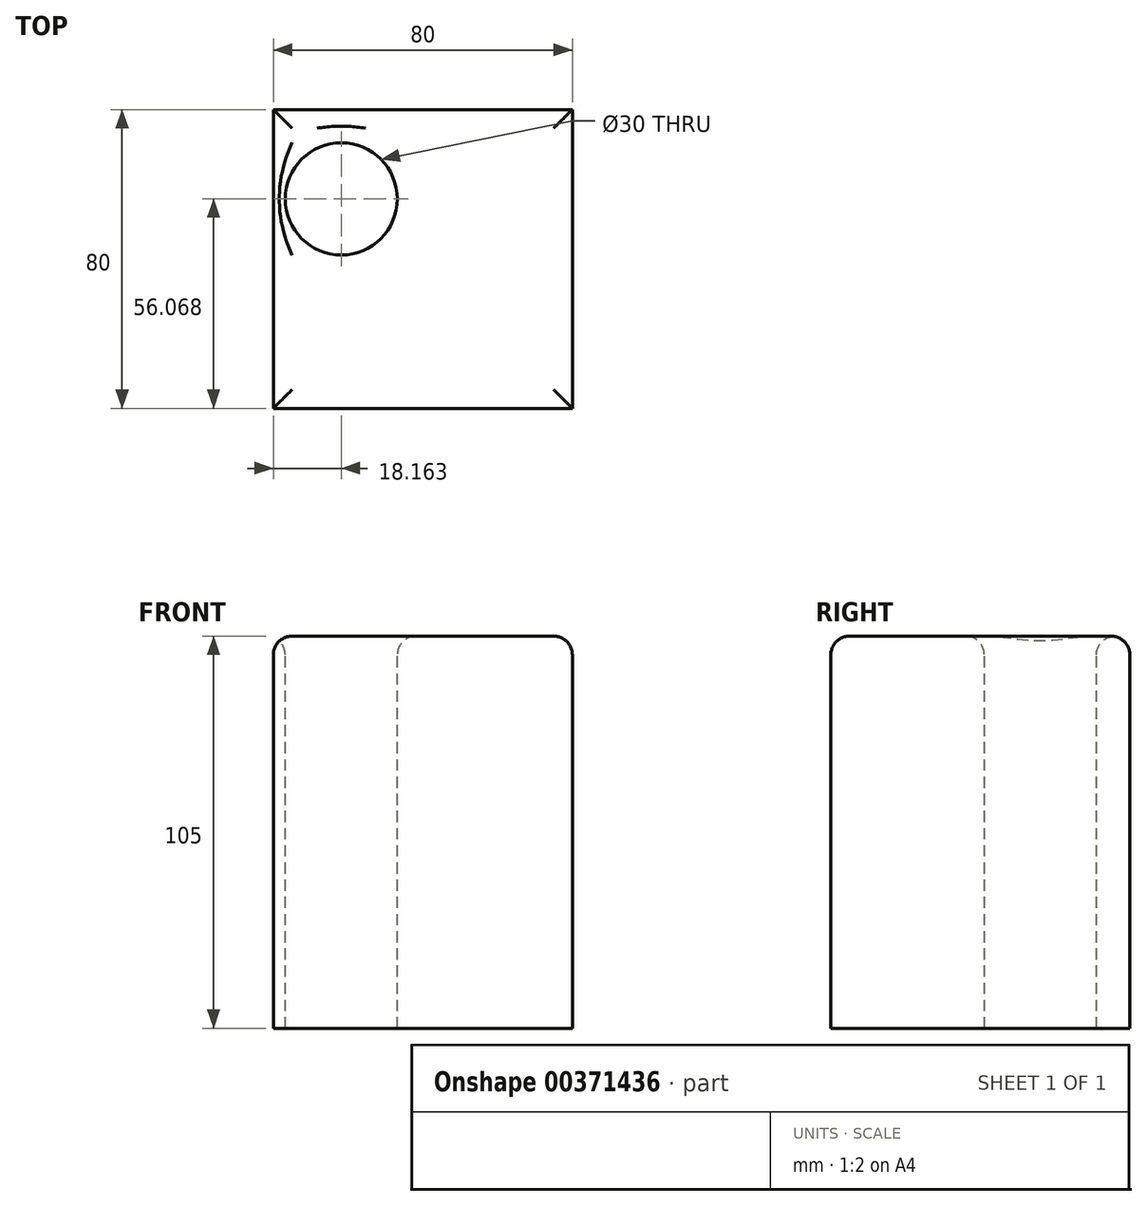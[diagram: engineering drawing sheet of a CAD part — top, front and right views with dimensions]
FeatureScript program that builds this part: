
annotation { "Feature Type Name" : "Feature", "Feature Type Description" : "" }
export const myFeature = defineFeature(function(context is Context, id is Id, definition is map)
    precondition{}
    {
        {
            var Q0;
            Q0=qCreatedBy(makeId("Top.planeOp"),FACE);
            var sketch = newSketch(context, id + "F0", { "sketchPlane" : qUnion([Q0])});
            skLineSegment(sketch, "E0.bottom", {"start": v(-141.9, 72.16) * mm, "end": v(-61.9, 72.16) * mm});
            skLineSegment(sketch, "E0.top", {"start": v(-141.9, -7.84) * mm, "end": v(-61.9, -7.84) * mm});
            skLineSegment(sketch, "E0.left", {"start": v(-141.9, 72.16) * mm, "end": v(-141.9, -7.84) * mm});
            skLineSegment(sketch, "E0.right", {"start": v(-61.9, 72.16) * mm, "end": v(-61.9, -7.84) * mm});
            skSolve(sketch);
        }
        {
            var Q0;
            Q0=makeQuery(id+"F0.imprint","IMPRINT",FACE,{"disambiguationData":[TD([[makeQuery(id+"F0.imprint","IMPRINT",EDGE,{"derivedFrom":sQuery(id+"F0.wireOp",EDGE,"E0.bottom")}),-1.0]])]});
            extrude(context, id + "F1", {"entities" : qUnion([Q0]), "depth" : 80 * mm});
        }
        {
            var Q0;
            Q0=makeQuery(id+"F1.opExtrude","CAP_FACE",FACE,{"disambiguationData":[OSD([sQuery(id+"F0.wireOp",EDGE,"E0.bottom"),sQuery(id+"F0.wireOp",EDGE,"E0.top"),sQuery(id+"F0.wireOp",EDGE,"E0.left"),sQuery(id+"F0.wireOp",EDGE,"E0.right")])],"isStart":false});
            extrude(context, id + "F2", {"entities" : qUnion([Q0]), "operationType" : NewBodyOperationType.ADD, "depth" : 25 * mm});
        }
        {
            var Q0;
            Q0=makeQuery(id+"F2.opExtrude","CAP_FACE",FACE,{"disambiguationData":[OSD([sQuery(id+"F0.wireOp",EDGE,"E0.bottom"),sQuery(id+"F0.wireOp",EDGE,"E0.top"),sQuery(id+"F0.wireOp",EDGE,"E0.left"),sQuery(id+"F0.wireOp",EDGE,"E0.right")])],"isStart":false});
            var sketch = newSketch(context, id + "F3", { "sketchPlane" : qUnion([Q0])});
            skCircle(sketch, "E1", {"center": v(-123.73, 48.23) * mm, "radius": 15 * mm});
            skSolve(sketch);
        }
        {
            var Q0;
            Q0=makeQuery(id+"F3.imprint","IMPRINT",FACE,{"disambiguationData":[TD([[makeQuery(id+"F3.imprint","IMPRINT",EDGE,{"derivedFrom":sQuery(id+"F3.wireOp",EDGE,"E1")}),1.0]])]});
            extrude(context, id + "F4", {"entities" : qUnion([Q0]), "operationType" : NewBodyOperationType.REMOVE, "endBound" : BoundingType.THROUGH_ALL, "oppositeDirection" : true, "depth" : 25 * mm});
        }
        {
            var Q0;
            Q0=makeQuery(id+"F4.boolean.opBoolean","COPY",EDGE,{"derivedFrom":makeQuery(id+"F4.opExtrude","CAP_EDGE",EDGE,{"disambiguationData":[OSD([sQuery(id+"F3.wireOp",EDGE,"E1")])],"isStart":true})});
            var Q1;
            Q1=makeQuery(id+"F2.opExtrude","CAP_FACE",FACE,{"disambiguationData":[OSD([sQuery(id+"F0.wireOp",EDGE,"E0.bottom"),sQuery(id+"F0.wireOp",EDGE,"E0.top"),sQuery(id+"F0.wireOp",EDGE,"E0.left"),sQuery(id+"F0.wireOp",EDGE,"E0.right")])],"isStart":false});
            fillet(context, id + "F5", {"entities" : qUnion([Q0, Q1]), "radius" : 5 * mm, "tangentPropagation" : true, "allowEdgeOverflow" : false});
        }
    });
